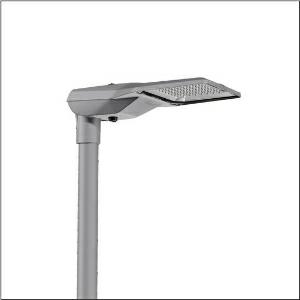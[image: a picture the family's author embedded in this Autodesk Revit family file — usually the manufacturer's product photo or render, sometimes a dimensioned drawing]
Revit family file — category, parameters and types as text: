
# Revit family: streetlight_sl_21_iq_midi___p0_5a_5xe3v31y08nb_ca8d
name_source: partatom
category: Lighting Fixtures
units: mm (PartAtom-declared; Revit-internal decimal feet)

## family parameters
Cut with Voids When Loaded = No
Host = Face
Light Source = No
Part Type = Normal
Room Calculation Point = No
Round Connector Dimension = Use Diameter
Shared = No

## types (1)
- --- (1 x LED, 21180 lm, 136.6 W, 3000K)
    Apparent Load = 137 VA
    CIE Flux Codes = 37 73 96 100 100
    Color Rendering = 70
    Color Temperature = 3000K
    Default Elevation = 1800 mm
    Description = Streetlight SL 21 iQ midi, mast luminaire, primary light control with lens, of PMMA, primary optical cover: cover, of toughened safety glass, transparent, light distribution: P0.5a, light emission: direct distribution, primary light characteristic: asymmetric, installation type: post-top, side-entry, LED, High Power LED, rated luminous flux: 21.180lm, luminous efficacy: 155lm/W, light colour: 730, colour temperature: 3000K, control gear: iQ-Street Remote, D4i with power reduction, control: pre-setting: logarithmic dimming characteristic, Street-Remote, Auto-Match, Temp-Guard, Lumen-Switch, Night-Set, Smart-Wire, Light-Fading, Desk-Remote (wireless, voltage-free reading and setting of iQ features in the workshop via application-optimized NFC function/RFID function), optimised constant luminous flux control (CLO 2.0), mains connection: 230..240V, AC, 50/60Hz, start of lifetime: 137W, end of service life: 144W, reduction: 61W, luminaire housing, of diecast aluminium, powder-coated, Siteco® metallic grey (DB 702S), corrosivity category C5 mid according to DIN EN ISO 12944, please order mast flange separately, inclination adjustable: 0°, 5°, 10°, 15°, sealing non-destructively replaceable, multi-level sealing system, length: 644mm, width: 335mm, height: 110mm, mast flange for spigot size: 42mm (side-entry): 5XC10008XM4, 60/48mm (side-entry/post-top): 5XC10108XM2, 76/60mm (side-entry/post-top): 5XC10108XM1, mounting height: 4..8m, Smart Interface below and above, protection rating (complete): IP66, insulation class (complete): insulation class II (safety insulation), certification: CE, ENEC, ENEC+, VDE, impact resistance: IK10, permissible operating ambient temperature for outdoor applications: -40..+50°C, standard-compliant lighting for roads and squares, packaging unit: 1 piece

Light Distribution: P0.5a
    Height = 111 mm
    Lamp = 1 x LED
    Lamp Light Flux = 21180 lm
    Lamp Power = 136.6 W
    Lamp count = 1
    Length = 644 mm
    Luminous efficacy = 155 lm/W
    Manufacturer = Siteco
    ModVariant = No
    Model = 5XE3V31Y08NB
    Number of Poles = 1
    OnlyDefault = Yes
    Power Factor = 1
    Product Name = Streetlight SL 21 iQ midi | P0.5a
    Product group = mast luminaire | pylon top
    ProductGroupID = 6100
    Protection Class = Protection class II
    Protection Degree = IP 66
    RLX_Detail_Level = 1
    RLX_Emergency_Light_Flux = 0 lm
    RLX_Emergency_Type = 0
    RLX_Emergency_Type_DB = No
    RlxData = <blob elided: 91173 chars, md5=7df1797d>
    Socket = socket
    Standby Power = 0 W
    System Light Flux = 21180 lm
    System Power = 137 W
    Type Comments = factory setting: luminous flux: 100 % | dim-lin: 254 | 733 mA
    Type Image = l_1004304.jpg
    URL = http://relux.com
    VarID = @adj_090797
    Voltage = 0 V
    Weight = 0.00 kg
    Width = 336 mm

## geometry (parser evidence)
native form markers: Blend x4, Sweep x11
no freeform markers — native parametric forms only
